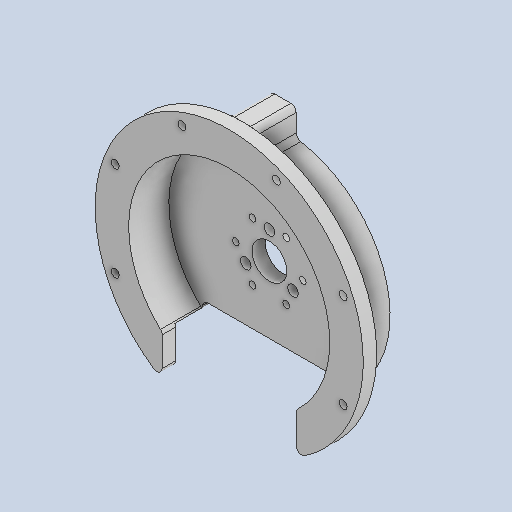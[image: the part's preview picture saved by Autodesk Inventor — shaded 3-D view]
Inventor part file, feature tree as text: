
AUTODESK INVENTOR PART (.ipt)
format: ipt  version: 2024.3 (Build 283343000, 343)  size: 233,984 bytes
history: native  units: mm
features: sketch x9, extrude x6, hole x3, fillet x2
ambient origin geometry x8: Origin, YZ Plane, XZ Plane, XY Plane, X Axis, Y Axis, Z Axis, Center Point
bodies: Body1 (feature_tree)
feature tree (20):
  extrude  "押し出し6"  Depth=80.0mm
  hole  "穴4"  [1 undecoded]
  hole  "穴5"  [1 undecoded]
  extrude  "押し出し7"  TaperAngle=30.0deg  [1 undecoded]
  extrude  "押し出し8"  Depth=60.0mm TaperAngle=360.0deg
  extrude  "押し出し9"  Depth=20.4mm
  hole  "穴6"  [1 undecoded]
  extrude  "押し出し10"  Depth=13.0mm
  fillet  "フィレット2"  [1 undecoded]
  extrude  "押し出し11"  Depth=100.0mm
  fillet  "フィレット3"  Radius=5.0mm
  sketch  "スケッチ9"
  sketch  "スケッチ10"
  sketch  "スケッチ11"
  sketch  "スケッチ12"
  sketch  "スケッチ13"
  sketch  "スケッチ14"
  sketch  "スケッチ15"
  sketch  "スケッチ16"
  sketch  "スケッチ17"
note: 5 required parameter values undecoded (feature->parameter linkage not recoverable at this tier; creation-order binding heuristic only, values carry confidence <= 0.55)
